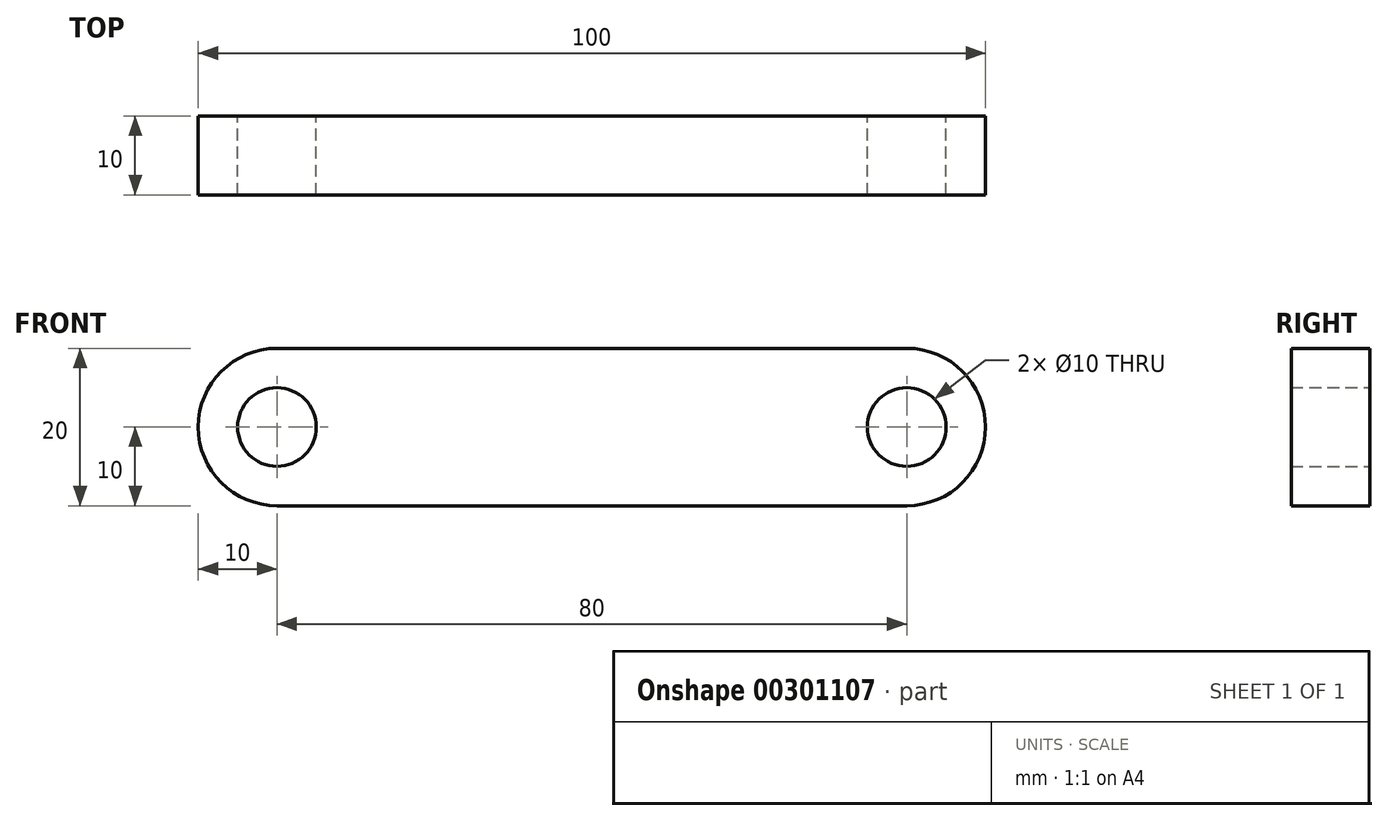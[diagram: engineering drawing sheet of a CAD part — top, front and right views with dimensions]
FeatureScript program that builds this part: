
annotation { "Feature Type Name" : "Feature", "Feature Type Description" : "" }
export const myFeature = defineFeature(function(context is Context, id is Id, definition is map)
    precondition{}
    {
        {
            var Q0;
            Q0=qCreatedBy(makeId("Front.planeOp"),FACE);
            var sketch = newSketch(context, id + "F0", { "sketchPlane" : qUnion([Q0])});
            skLineSegment(sketch, "E0.bottom", {"start": v(10, 0) * mm, "end": v(90, 0) * mm});
            skLineSegment(sketch, "E0.top", {"start": v(10, 20) * mm, "end": v(90, 20) * mm});
            skLineSegment(sketch, "E0.left", {"start": v(0, 10) * mm, "end": v(0, 10) * mm});
            skLineSegment(sketch, "E0.right", {"start": v(100, 10) * mm, "end": v(100, 10) * mm});
            skPoint(sketch, "E1.visualSharp", {"position": v(0, 20) * mm});
            skArc(sketch, "E1.filletArc", {"start": v(10, 20) * mm, "mid": v(2.93, 17.07) * mm, "end": v(0, 10) * mm});
            skPoint(sketch, "E2.visualSharp", {"position": v(0, 0) * mm});
            skArc(sketch, "E2.filletArc", {"start": v(0, 10) * mm, "mid": v(2.93, 2.93) * mm, "end": v(10, 0) * mm});
            skPoint(sketch, "E3.visualSharp", {"position": v(100, 20) * mm});
            skArc(sketch, "E3.filletArc", {"start": v(100, 10) * mm, "mid": v(97.07, 17.07) * mm, "end": v(90, 20) * mm});
            skPoint(sketch, "E4.visualSharp", {"position": v(100, 0) * mm});
            skArc(sketch, "E4.filletArc", {"start": v(90, 0) * mm, "mid": v(97.07, 2.93) * mm, "end": v(100, 10) * mm});
            skCircle(sketch, "E5", {"center": v(10, 10) * mm, "radius": 5 * mm});
            skCircle(sketch, "E6", {"center": v(90, 10) * mm, "radius": 5 * mm});
            skSolve(sketch);
        }
        {
            var Q0;
            Q0=makeQuery(id+"F0.imprint","IMPRINT",FACE,{"disambiguationData":[TD([[makeQuery(id+"F0.imprint","IMPRINT",EDGE,{"derivedFrom":sQuery(id+"F0.wireOp",EDGE,"E0.bottom")}),1.0]])]});
            extrude(context, id + "F1", {"entities" : qUnion([Q0]), "depth" : 10 * mm});
        }
    });
